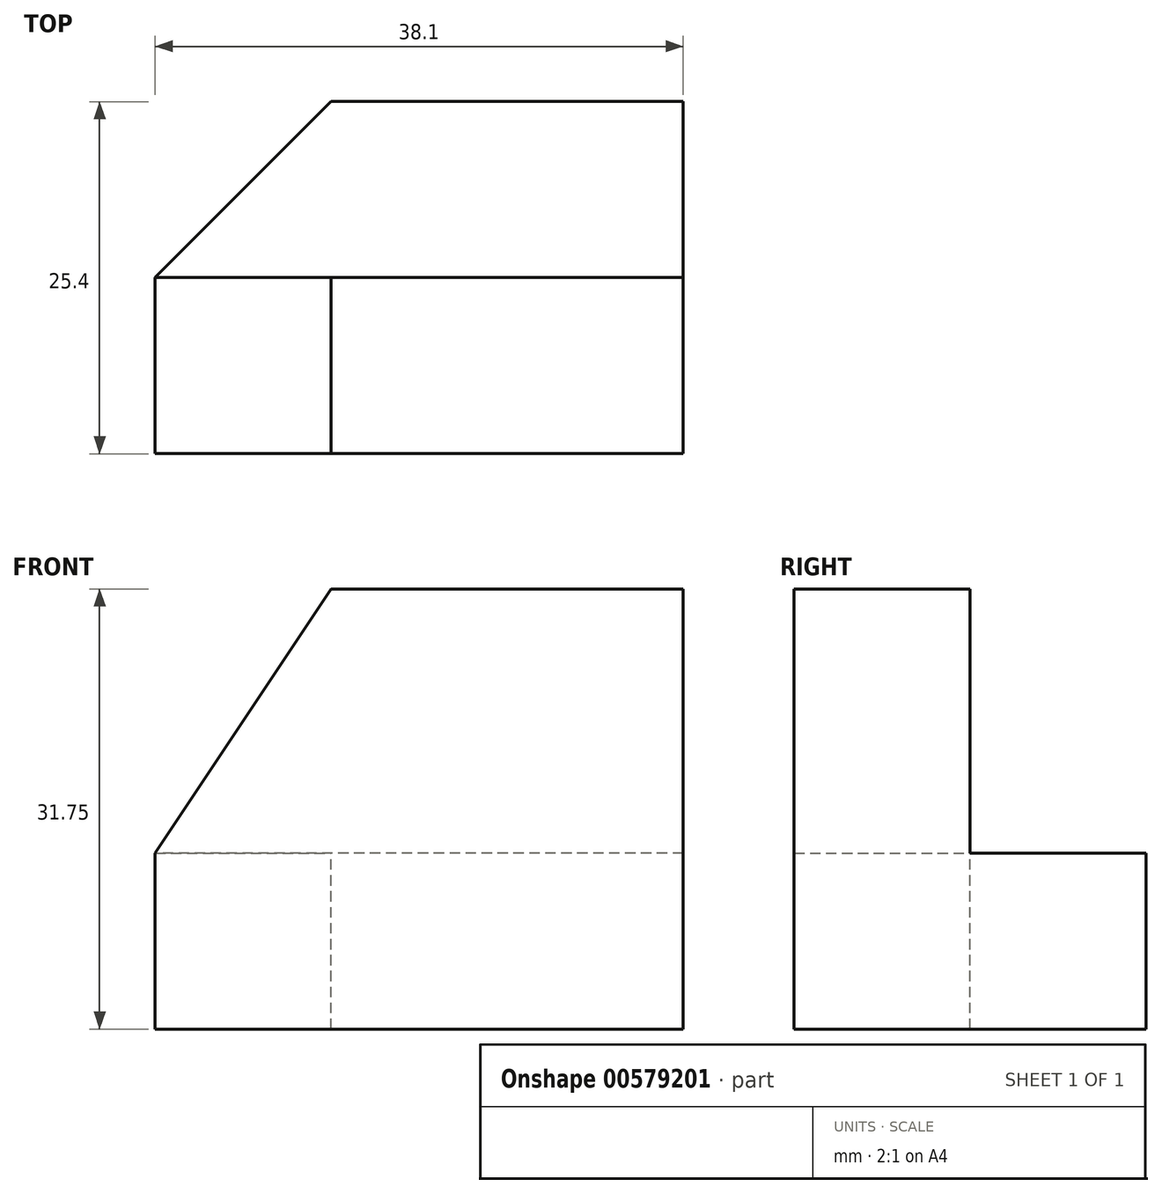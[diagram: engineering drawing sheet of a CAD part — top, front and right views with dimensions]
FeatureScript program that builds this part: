
annotation { "Feature Type Name" : "Feature", "Feature Type Description" : "" }
export const myFeature = defineFeature(function(context is Context, id is Id, definition is map)
    precondition{}
    {
        {
            var Q0;
            Q0=qCreatedBy(makeId("Right.planeOp"),FACE);
            var sketch = newSketch(context, id + "F0", { "sketchPlane" : qUnion([Q0])});
            skLineSegment(sketch, "E0", {"start": v(-57.52, 56.25) * mm, "end": v(-57.52, 24.5) * mm});
            skLineSegment(sketch, "E1", {"start": v(-57.52, 24.5) * mm, "end": v(-32.12, 24.5) * mm});
            skLineSegment(sketch, "E2", {"start": v(-32.12, 24.5) * mm, "end": v(-32.12, 37.2) * mm});
            skLineSegment(sketch, "E3", {"start": v(-32.12, 37.2) * mm, "end": v(-44.82, 37.2) * mm});
            skLineSegment(sketch, "E4", {"start": v(-44.82, 37.2) * mm, "end": v(-44.82, 56.25) * mm});
            skLineSegment(sketch, "E5", {"start": v(-44.82, 56.25) * mm, "end": v(-57.52, 56.25) * mm});
            skSolve(sketch);
        }
        {
            var Q0;
            Q0 = qSketchRegion(id + "F0", true);
            extrude(context, id + "F1", {"entities" : qUnion([Q0]), "depth" : 38.1 * mm, "offsetDistance" : 25.4 * mm});
        }
        {
            var Q0;
            Q0=makeQuery(id+"F1.opExtrude","SWEPT_FACE",FACE,{"disambiguationData":[OSD([sQuery(id+"F0.wireOp",EDGE,"E4")])]});
            var sketch = newSketch(context, id + "F2", { "sketchPlane" : qUnion([Q0])});
            skLineSegment(sketch, "E6", {"start": v(-12.7, 56.25) * mm, "end": v(0, 37.2) * mm});
            skLineSegment(sketch, "E7", {"start": v(0, 37.2) * mm, "end": v(0, 56.25) * mm});
            skLineSegment(sketch, "E8", {"start": v(0, 56.25) * mm, "end": v(-12.7, 56.25) * mm});
            skSolve(sketch);
        }
        {
            var Q0;
            Q0=makeQuery(id+"F2.imprint","IMPRINT",FACE,{"disambiguationData":[TD([[makeQuery(id+"F2.imprint","IMPRINT",EDGE,{"derivedFrom":sQuery(id+"F2.wireOp",EDGE,"E6")}),1.0]])]});
            extrude(context, id + "F3", {"entities" : qUnion([Q0]), "operationType" : NewBodyOperationType.REMOVE, "oppositeDirection" : true, "depth" : 12.7 * mm, "offsetDistance" : 25.4 * mm});
        }
        {
            var Q0;
            Q0=makeQuery(id+"F1.opExtrude","SWEPT_FACE",FACE,{"disambiguationData":[OSD([sQuery(id+"F0.wireOp",EDGE,"E3")])]});
            var sketch = newSketch(context, id + "F4", { "sketchPlane" : qUnion([Q0])});
            skLineSegment(sketch, "E9", {"start": v(0, -44.82) * mm, "end": v(12.7, -32.12) * mm});
            skLineSegment(sketch, "E10", {"start": v(12.7, -32.12) * mm, "end": v(0, -32.12) * mm});
            skLineSegment(sketch, "E11", {"start": v(0, -32.12) * mm, "end": v(0, -44.82) * mm});
            skSolve(sketch);
        }
        {
            var Q0;
            Q0 = qSketchRegion(id + "F4", true);
            extrude(context, id + "F5", {"entities" : qUnion([Q0]), "operationType" : NewBodyOperationType.REMOVE, "oppositeDirection" : true, "depth" : 25.4 * mm, "offsetDistance" : 25.4 * mm});
        }
    });
